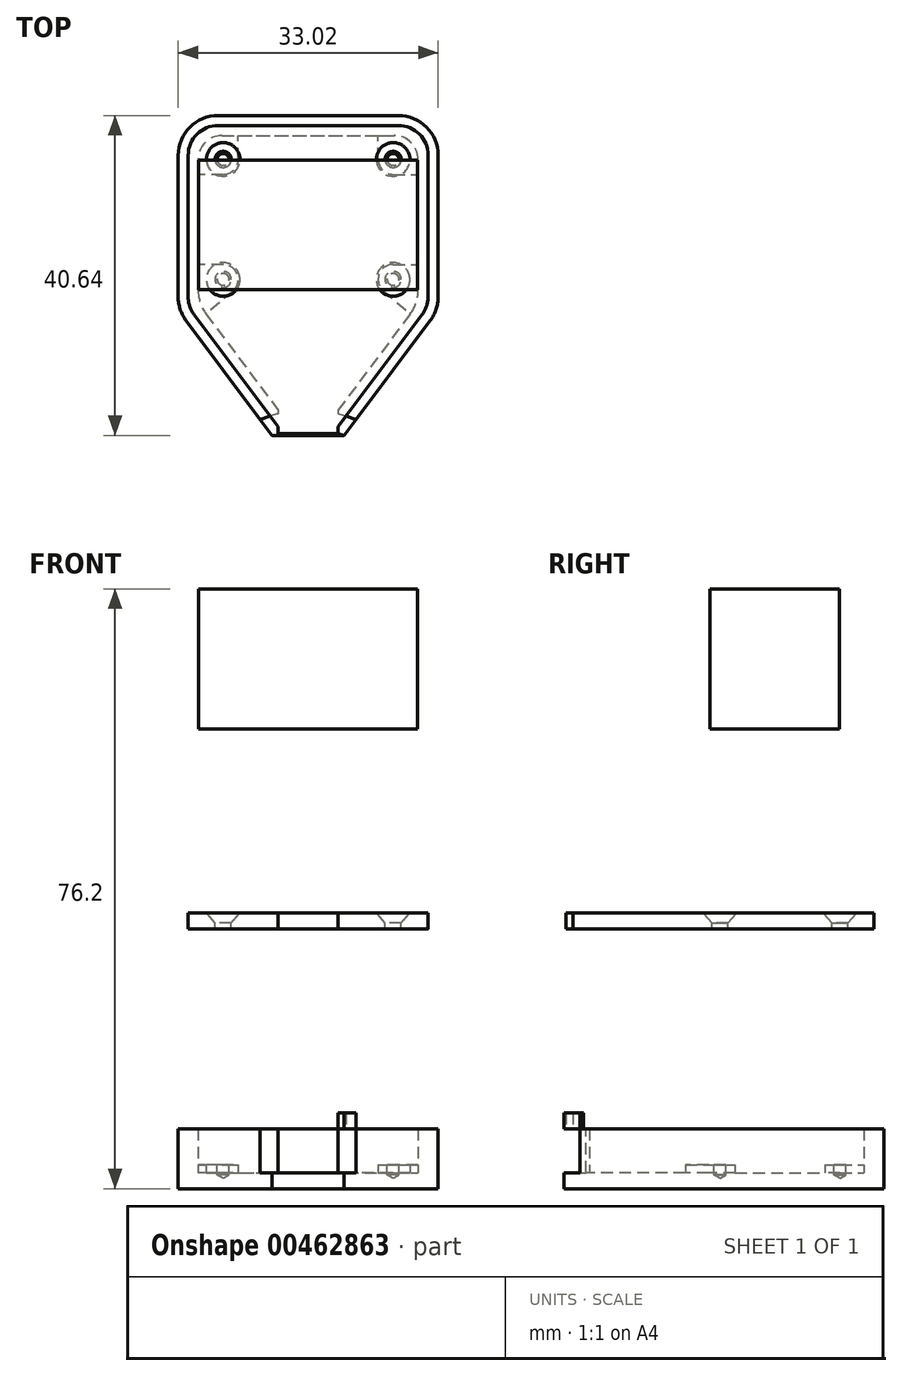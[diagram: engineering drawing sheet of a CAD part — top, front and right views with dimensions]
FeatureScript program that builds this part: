
annotation { "Feature Type Name" : "Feature", "Feature Type Description" : "" }
export const myFeature = defineFeature(function(context is Context, id is Id, definition is map)
    precondition{}
    {
        {
            var Q0;
            Q0=qCreatedBy(makeId("Top.planeOp"),FACE);
            var sketch = newSketch(context, id + "F0", { "sketchPlane" : qUnion([Q0])});
            skLineSegment(sketch, "E0.right", {"start": v(-13.97, -10.67) * mm, "end": v(-13.97, 10.67) * mm});
            skLineSegment(sketch, "E1", {"start": v(-13.97, -10.67) * mm, "end": v(-3.81, -24.21) * mm});
            skLineSegment(sketch, "E2", {"start": v(-3.81, -24.21) * mm, "end": v(-3.81, -28.45) * mm});
            skLineSegment(sketch, "E3", {"start": v(-3.8, -28.45) * mm, "end": v(-16.51, -11.51) * mm});
            skLineSegment(sketch, "E4", {"start": v(-16.51, -11.51) * mm, "end": v(-16.51, 13.2) * mm});
            skLineSegment(sketch, "E5", {"start": v(-13.97, 10.67) * mm, "end": v(0, 10.67) * mm});
            skLineSegment(sketch, "E6", {"start": v(-16.51, 13.2) * mm, "end": v(0, 13.2) * mm});
            skLineSegment(sketch, "E7", {"start": v(0, 10.67) * mm, "end": v(0, 13.2) * mm, "construction": true});
            skLineSegment(sketch, "E8", {"start": v(-13.97, 0) * mm, "end": v(-16.51, 0) * mm, "construction": true});
            skLineSegment(sketch, "E9", {"start": v(-8.9, -17.44) * mm, "end": v(-10.92, -18.97) * mm, "construction": true});
            skLineSegment(sketch, "E10", {"start": v(-13.97, -10.67) * mm, "end": v(0, -10.67) * mm, "construction": true});
            skLineSegment(sketch, "E11", {"start": v(0, -10.67) * mm, "end": v(0, -28.45) * mm, "construction": true});
            skLineSegment(sketch, "E12", {"start": v(0, -28.45) * mm, "end": v(-3.8, -28.45) * mm});
            skLineSegment(sketch, "E13", {"start": v(0, 10.16) * mm, "end": v(0, -10.67) * mm, "construction": true});
            skLineSegment(sketch, "E14.MirrorCS", {"start": v(16.51, 13.2) * mm, "end": v(0, 13.2) * mm});
            skLineSegment(sketch, "E15.MirrorCS", {"start": v(13.97, 10.67) * mm, "end": v(0, 10.67) * mm});
            skLineSegment(sketch, "E16.MirrorCS", {"start": v(16.51, -11.51) * mm, "end": v(16.51, 13.2) * mm});
            skLineSegment(sketch, "E17.MirrorCS", {"start": v(13.97, -10.67) * mm, "end": v(13.97, 10.67) * mm});
            skLineSegment(sketch, "E18.MirrorCS", {"start": v(13.97, -10.67) * mm, "end": v(3.81, -24.21) * mm});
            skLineSegment(sketch, "E19.MirrorCS", {"start": v(3.8, -28.45) * mm, "end": v(16.51, -11.51) * mm});
            skLineSegment(sketch, "E20.MirrorCS", {"start": v(3.81, -24.21) * mm, "end": v(3.81, -28.45) * mm});
            skLineSegment(sketch, "E21.MirrorCS", {"start": v(0, -28.45) * mm, "end": v(3.81, -28.45) * mm});
            skLineSegment(sketch, "E22", {"start": v(13.46, 0) * mm, "end": v(-13.46, 0) * mm, "construction": true});
            skLineSegment(sketch, "E23", {"start": v(-3.81, -24.21) * mm, "end": v(3.81, -24.21) * mm, "construction": true});
            skLineSegment(sketch, "E24", {"start": v(-13.46, 7.62) * mm, "end": v(-10.8, 7.62) * mm, "construction": true});
            skLineSegment(sketch, "E25", {"start": v(-10.8, 7.62) * mm, "end": v(-10.8, 10.16) * mm, "construction": true});
            skLineSegment(sketch, "E26.bottom", {"start": v(-10.92, 10.16) * mm, "end": v(13.46, 10.16) * mm, "construction": true});
            skLineSegment(sketch, "E26.top", {"start": v(-13.46, -10.16) * mm, "end": v(13.46, -10.16) * mm, "construction": true});
            skLineSegment(sketch, "E26.left", {"start": v(-13.46, 7.62) * mm, "end": v(-13.46, -10.16) * mm, "construction": true});
            skLineSegment(sketch, "E26.right", {"start": v(13.46, 10.16) * mm, "end": v(13.46, -10.16) * mm, "construction": true});
            skPoint(sketch, "E26.middle", {"position": v(0, 0) * mm});
            skLineSegment(sketch, "E27", {"start": v(-13.46, 0) * mm, "end": v(-13.97, 0) * mm, "construction": true});
            skLineSegment(sketch, "E28.bottom", {"start": v(0, 10.67) * mm, "end": v(0, 10.67) * mm});
            skLineSegment(sketch, "E28.top", {"start": v(0, 10.16) * mm, "end": v(0, 10.16) * mm});
            skLineSegment(sketch, "E28.left", {"start": v(0, 10.67) * mm, "end": v(0, 10.16) * mm, "construction": true});
            skLineSegment(sketch, "E28.right", {"start": v(0, 10.67) * mm, "end": v(0, 10.16) * mm, "construction": true});
            skPoint(sketch, "E29.visualSharp", {"position": v(-13.46, 10.16) * mm});
            skArc(sketch, "E29.filletArc", {"start": v(-10.92, 10.16) * mm, "mid": v(-12.72, 9.42) * mm, "end": v(-13.46, 7.62) * mm, "construction": true});
            skSolve(sketch);
        }
        {
            var Q0;
            Q0=makeQuery(id+"F0.imprint","IMPRINT",FACE,{"disambiguationData":[TD([[makeQuery(id+"F0.imprint","IMPRINT",EDGE,{"derivedFrom":sQuery(id+"F0.wireOp",EDGE,"E0.right")}),1.0]])]});
            extrude(context, id + "F1", {"entities" : qUnion([Q0]), "depth" : 5.6 * mm});
        }
        {
            var Q0;
            {var subQ0=sQuery(id+"F0.wireOp",EDGE,"E16.MirrorCS");var subQ1=sQuery(id+"F0.wireOp",EDGE,"E14.MirrorCS");Q0=makeQuery(id+"F1.boolean.opBoolean","MERGE",EDGE,{"derivedFrom":[makeQuery(id+"Ff96gasZhOdMvVI_0.opExtrude","SWEPT_EDGE",EDGE,{"disambiguationData":[OSD([subQ1,subQ0])]}),makeQuery(id+"F1.opExtrude","SWEPT_EDGE",EDGE,{"disambiguationData":[OSD([subQ1,subQ0])]})]});}
            var Q1;
            {var subQ0=sQuery(id+"F0.wireOp",EDGE,"E6");var subQ1=sQuery(id+"F0.wireOp",EDGE,"E4");Q1=makeQuery(id+"F1.boolean.opBoolean","MERGE",EDGE,{"derivedFrom":[makeQuery(id+"Ff96gasZhOdMvVI_0.opExtrude","SWEPT_EDGE",EDGE,{"disambiguationData":[OSD([subQ1,subQ0])]}),makeQuery(id+"F1.opExtrude","SWEPT_EDGE",EDGE,{"disambiguationData":[OSD([subQ1,subQ0])]})]});}
            var Q2;
            {var subQ0=sQuery(id+"F0.wireOp",EDGE,"E19.MirrorCS");var subQ1=sQuery(id+"F0.wireOp",EDGE,"E16.MirrorCS");Q2=makeQuery(id+"F1.boolean.opBoolean","MERGE",EDGE,{"derivedFrom":[makeQuery(id+"Ff96gasZhOdMvVI_0.opExtrude","SWEPT_EDGE",EDGE,{"disambiguationData":[OSD([subQ1,subQ0])]}),makeQuery(id+"F1.opExtrude","SWEPT_EDGE",EDGE,{"disambiguationData":[OSD([subQ1,subQ0])]})]});}
            var Q3;
            Q3=makeQuery(id+"F1.opExtrude","SWEPT_EDGE",EDGE,{"disambiguationData":[OSD([sQuery(id+"F0.wireOp",EDGE,"E0.right"),sQuery(id+"F0.wireOp",EDGE,"E1")])]});
            var Q4;
            Q4=makeQuery(id+"F1.opExtrude","SWEPT_EDGE",EDGE,{"disambiguationData":[OSD([sQuery(id+"F0.wireOp",EDGE,"E17.MirrorCS"),sQuery(id+"F0.wireOp",EDGE,"E18.MirrorCS")])]});
            var Q5;
            {var subQ0=sQuery(id+"F0.wireOp",EDGE,"E4");var subQ1=sQuery(id+"F0.wireOp",EDGE,"E3");Q5=makeQuery(id+"F1.boolean.opBoolean","MERGE",EDGE,{"derivedFrom":[makeQuery(id+"Ff96gasZhOdMvVI_0.opExtrude","SWEPT_EDGE",EDGE,{"disambiguationData":[OSD([subQ1,subQ0])]}),makeQuery(id+"F1.opExtrude","SWEPT_EDGE",EDGE,{"disambiguationData":[OSD([subQ1,subQ0])]})]});}
            fillet(context, id + "F2", {"entities" : qUnion([Q0, Q1, Q2, Q3, Q4, Q5]), "radius" : 5.08 * mm, "tangentPropagation" : true, "allowEdgeOverflow" : false});
        }
        {
            var Q0;
            Q0=makeQuery(id+"F1.opExtrude","SWEPT_EDGE",EDGE,{"disambiguationData":[OSD([sQuery(id+"F0.wireOp",EDGE,"E0.right"),sQuery(id+"F0.wireOp",EDGE,"E5")])]});
            var Q1;
            Q1=makeQuery(id+"F1.opExtrude","SWEPT_EDGE",EDGE,{"disambiguationData":[OSD([sQuery(id+"F0.wireOp",EDGE,"E15.MirrorCS"),sQuery(id+"F0.wireOp",EDGE,"E17.MirrorCS")])]});
            fillet(context, id + "F3", {"entities" : qUnion([Q0, Q1]), "radius" : 3.05 * mm, "tangentPropagation" : true, "allowEdgeOverflow" : false});
        }
        {
            var Q0;
            Q0=makeQuery(id+"F1.opExtrude","SWEPT_EDGE",EDGE,{"disambiguationData":[OSD([sQuery(id+"F0.wireOp",EDGE,"E19.MirrorCS"),sQuery(id+"F0.wireOp",EDGE,"E20.MirrorCS"),sQuery(id+"F0.wireOp",EDGE,"E21.MirrorCS")])]});
            var Q1;
            Q1=makeQuery(id+"F1.opExtrude","SWEPT_EDGE",EDGE,{"disambiguationData":[OSD([sQuery(id+"F0.wireOp",EDGE,"E2"),sQuery(id+"F0.wireOp",EDGE,"E3"),sQuery(id+"F0.wireOp",EDGE,"E12")])]});
            chamfer(context, id + "F4", {"entities" : qUnion([Q0, Q1]), "width" : 1.27 * mm, "tangentPropagation" : true});
        }
        {
            var Q0;
            Q0=makeQuery(id+"F1.opExtrude","CAP_FACE",FACE,{"disambiguationData":[OSD([sQuery(id+"F0.wireOp",EDGE,"E0.right"),sQuery(id+"F0.wireOp",EDGE,"E1"),sQuery(id+"F0.wireOp",EDGE,"E2"),sQuery(id+"F0.wireOp",EDGE,"E3"),sQuery(id+"F0.wireOp",EDGE,"E4"),sQuery(id+"F0.wireOp",EDGE,"E5"),sQuery(id+"F0.wireOp",EDGE,"E6"),sQuery(id+"F0.wireOp",EDGE,"E14.MirrorCS"),sQuery(id+"F0.wireOp",EDGE,"E15.MirrorCS"),sQuery(id+"F0.wireOp",EDGE,"E16.MirrorCS"),sQuery(id+"F0.wireOp",EDGE,"E17.MirrorCS"),sQuery(id+"F0.wireOp",EDGE,"E18.MirrorCS"),sQuery(id+"F0.wireOp",EDGE,"E19.MirrorCS"),sQuery(id+"F0.wireOp",EDGE,"E20.MirrorCS")])],"isStart":true});
            var sketch = newSketch(context, id + "F5", { "sketchPlane" : qUnion([Q0])});
            skArc(sketch, "E30.0", {"start": v(16.51, 9.82) * mm, "mid": v(16.25, 11.43) * mm, "end": v(15.5, 12.87) * mm});
            skLineSegment(sketch, "E31.0", {"start": v(16.51, 9.82) * mm, "end": v(16.51, -8.13) * mm});
            skArc(sketch, "E32.0", {"start": v(11.43, -13.2) * mm, "mid": v(15.02, -11.72) * mm, "end": v(16.51, -8.13) * mm});
            skLineSegment(sketch, "E33.0", {"start": v(11.43, -13.2) * mm, "end": v(-11.43, -13.2) * mm});
            skArc(sketch, "E34.0", {"start": v(-16.51, -8.13) * mm, "mid": v(-15.02, -11.72) * mm, "end": v(-11.43, -13.2) * mm});
            skLineSegment(sketch, "E35.0", {"start": v(-16.51, 9.82) * mm, "end": v(-16.51, -8.13) * mm});
            skArc(sketch, "E36.0", {"start": v(-15.5, 12.87) * mm, "mid": v(-16.25, 11.43) * mm, "end": v(-16.51, 9.82) * mm});
            skLineSegment(sketch, "E37.0", {"start": v(4.57, 27.43) * mm, "end": v(15.5, 12.87) * mm});
            skLineSegment(sketch, "E38.0", {"start": v(-4.57, 27.43) * mm, "end": v(-15.5, 12.87) * mm});
            skLineSegment(sketch, "E39", {"start": v(4.57, 27.43) * mm, "end": v(-4.57, 27.43) * mm});
            skSolve(sketch);
        }
        {
            var Q0;
            Q0 = qSketchRegion(id + "F5", true);
            extrude(context, id + "F6", {"entities" : qUnion([Q0]), "operationType" : NewBodyOperationType.ADD, "depth" : 2.03 * mm});
        }
        {
            var Q0;
            Q0=makeQuery(id+"F1.opExtrude","CAP_FACE",FACE,{"disambiguationData":[OSD([sQuery(id+"F0.wireOp",EDGE,"E0.right"),sQuery(id+"F0.wireOp",EDGE,"E1"),sQuery(id+"F0.wireOp",EDGE,"E2"),sQuery(id+"F0.wireOp",EDGE,"E3"),sQuery(id+"F0.wireOp",EDGE,"E4"),sQuery(id+"F0.wireOp",EDGE,"E5"),sQuery(id+"F0.wireOp",EDGE,"E6"),sQuery(id+"F0.wireOp",EDGE,"E14.MirrorCS"),sQuery(id+"F0.wireOp",EDGE,"E15.MirrorCS"),sQuery(id+"F0.wireOp",EDGE,"E16.MirrorCS"),sQuery(id+"F0.wireOp",EDGE,"E17.MirrorCS"),sQuery(id+"F0.wireOp",EDGE,"E18.MirrorCS"),sQuery(id+"F0.wireOp",EDGE,"E19.MirrorCS"),sQuery(id+"F0.wireOp",EDGE,"E20.MirrorCS")])],"isStart":false});
            var sketch = newSketch(context, id + "F7", { "sketchPlane" : qUnion([Q0])});
            skLineSegment(sketch, "E40.0", {"start": v(4.57, -27.43) * mm, "end": v(15.5, -12.87) * mm});
            skArc(sketch, "E41.0", {"start": v(15.5, -12.87) * mm, "mid": v(16.25, -11.43) * mm, "end": v(16.51, -9.82) * mm});
            skLineSegment(sketch, "E42.0", {"start": v(16.51, -9.82) * mm, "end": v(16.51, 8.13) * mm});
            skArc(sketch, "E43.0", {"start": v(16.51, 8.13) * mm, "mid": v(15.02, 11.72) * mm, "end": v(11.43, 13.2) * mm});
            skLineSegment(sketch, "E44.0", {"start": v(11.43, 13.2) * mm, "end": v(-11.43, 13.2) * mm});
            skArc(sketch, "E45.0", {"start": v(-11.43, 13.2) * mm, "mid": v(-15.02, 11.72) * mm, "end": v(-16.51, 8.13) * mm});
            skLineSegment(sketch, "E46.0", {"start": v(-16.51, -9.82) * mm, "end": v(-16.51, 8.13) * mm});
            skArc(sketch, "E47.0", {"start": v(-16.51, -9.82) * mm, "mid": v(-16.25, -11.43) * mm, "end": v(-15.5, -12.87) * mm});
            skLineSegment(sketch, "E48.0", {"start": v(-4.57, -27.43) * mm, "end": v(-15.5, -12.87) * mm});
            skLineSegment(sketch, "E49", {"start": v(-4.57, -27.43) * mm, "end": v(-3.81, -27.18) * mm});
            skLineSegment(sketch, "E50", {"start": v(3.81, -27.18) * mm, "end": v(4.57, -27.43) * mm});
            skLineSegment(sketch, "E51.0", {"start": v(3.81, -26.33) * mm, "end": v(14.48, -12.1) * mm});
            skArc(sketch, "E51.1", {"start": v(14.48, -12.1) * mm, "mid": v(15.04, -11.03) * mm, "end": v(15.24, -9.82) * mm});
            skLineSegment(sketch, "E51.2", {"start": v(15.24, -9.82) * mm, "end": v(15.24, 8.13) * mm});
            skArc(sketch, "E51.3", {"start": v(15.24, 8.13) * mm, "mid": v(14.12, 10.82) * mm, "end": v(11.43, 11.94) * mm});
            skLineSegment(sketch, "E51.4", {"start": v(11.43, 11.94) * mm, "end": v(-11.43, 11.94) * mm});
            skLineSegment(sketch, "E51.5", {"start": v(-3.81, -26.33) * mm, "end": v(-14.48, -12.1) * mm});
            skArc(sketch, "E51.6", {"start": v(-15.24, -9.82) * mm, "mid": v(-15.04, -11.03) * mm, "end": v(-14.48, -12.1) * mm});
            skLineSegment(sketch, "E51.7", {"start": v(-15.24, -9.82) * mm, "end": v(-15.24, 8.13) * mm});
            skArc(sketch, "E51.8", {"start": v(-11.43, 11.94) * mm, "mid": v(-14.12, 10.82) * mm, "end": v(-15.24, 8.13) * mm});
            skLineSegment(sketch, "E52", {"start": v(-3.8, -26.33) * mm, "end": v(-3.8, -27.18) * mm});
            skLineSegment(sketch, "E53", {"start": v(3.8, -26.33) * mm, "end": v(3.81, -27.18) * mm});
            skSolve(sketch);
        }
        {
            var Q0;
            Q0=makeQuery(id+"F7.imprint","IMPRINT",FACE,{"disambiguationData":[TD([[makeQuery(id+"F7.imprint","IMPRINT",EDGE,{"derivedFrom":sQuery(id+"F7.wireOp",EDGE,"E40.0")}),1.0]])]});
            extrude(context, id + "F8", {"entities" : qUnion([Q0]), "operationType" : NewBodyOperationType.ADD, "depth" : 2.03 * mm});
        }
        {
            var Q0;
            Q0=makeQuery(id+"F6.opExtrude","CAP_FACE",FACE,{"disambiguationData":[OSD([sQuery(id+"F5.wireOp",EDGE,"614055ea-427b-4cb9-ac48-1e12848c68dc.0"),sQuery(id+"F5.wireOp",EDGE,"E30.0"),sQuery(id+"F5.wireOp",EDGE,"E31.0"),sQuery(id+"F5.wireOp",EDGE,"E32.0"),sQuery(id+"F5.wireOp",EDGE,"E33.0"),sQuery(id+"F5.wireOp",EDGE,"E34.0"),sQuery(id+"F5.wireOp",EDGE,"E35.0"),sQuery(id+"F5.wireOp",EDGE,"E36.0"),sQuery(id+"F5.wireOp",EDGE,"936ec802-ce90-48c8-9038-d904150573fe.0"),sQuery(id+"F5.wireOp",EDGE,"719f3388-4424-430d-82b7-2a579ba14330.0"),sQuery(id+"F5.wireOp",EDGE,"24262252-db0e-4c5c-9644-e6070294630f.0"),sQuery(id+"F5.wireOp",EDGE,"891P9168-ehHu-ZQn1-B7PZ-iqxXZud2gJmg")])],"isStart":true});
            var sketch = newSketch(context, id + "F9", { "sketchPlane" : qUnion([Q0])});
            skPoint(sketch, "E54.0", {"position": v(-10.8, 7.62) * mm});
            skLineSegment(sketch, "E55.0", {"start": v(0, 10.16) * mm, "end": v(0, -10.67) * mm, "construction": true});
            skLineSegment(sketch, "E56.0", {"start": v(13.46, 0) * mm, "end": v(-13.46, 0) * mm, "construction": true});
            skCircle(sketch, "E57", {"center": v(-10.8, 7.62) * mm, "radius": 1.9 * mm});
            skCircle(sketch, "E58.MirrorC", {"center": v(10.8, 7.62) * mm, "radius": 1.9 * mm});
            skCircle(sketch, "E59.MirrorC", {"center": v(-10.8, -7.62) * mm, "radius": 1.9 * mm});
            skCircle(sketch, "E60.MirrorC", {"center": v(10.8, -7.62) * mm, "radius": 1.9 * mm});
            skLineSegment(sketch, "E61", {"start": v(-8.9, 7.62) * mm, "end": v(-8.9, 10.67) * mm});
            skLineSegment(sketch, "E62", {"start": v(-10.8, 5.71) * mm, "end": v(-13.97, 5.71) * mm});
            skLineSegment(sketch, "E63", {"start": v(-10.8, -5.72) * mm, "end": v(-13.97, -5.72) * mm});
            skLineSegment(sketch, "E64", {"start": v(-9.54, -9.06) * mm, "end": v(-12.95, -12.02) * mm});
            skLineSegment(sketch, "E65.MirrorCS", {"start": v(8.9, 7.62) * mm, "end": v(8.9, 10.67) * mm});
            skLineSegment(sketch, "E66.MirrorCS", {"start": v(10.8, 5.71) * mm, "end": v(13.97, 5.71) * mm});
            skLineSegment(sketch, "E67.MirrorCS", {"start": v(10.8, -5.72) * mm, "end": v(13.97, -5.72) * mm});
            skLineSegment(sketch, "E68.MirrorCS", {"start": v(9.54, -9.06) * mm, "end": v(12.95, -12.02) * mm});
            skCircle(sketch, "E69", {"center": v(-10.8, 7.62) * mm, "radius": 1.14 * mm, "construction": true});
            skCircle(sketch, "E70.MirrorC", {"center": v(10.8, 7.62) * mm, "radius": 1.14 * mm, "construction": true});
            skCircle(sketch, "E71.MirrorC", {"center": v(-10.8, -7.62) * mm, "radius": 1.14 * mm, "construction": true});
            skCircle(sketch, "E72.MirrorC", {"center": v(10.8, -7.62) * mm, "radius": 1.14 * mm, "construction": true});
            skPoint(sketch, "E73", {"position": v(-9.65, 7.62) * mm});
            skPoint(sketch, "E74", {"position": v(-10.8, 8.76) * mm});
            skPoint(sketch, "E75", {"position": v(-10.8, 6.48) * mm});
            skPoint(sketch, "E76", {"position": v(-11.94, 7.62) * mm});
            skPoint(sketch, "E77.MirrorP", {"position": v(11.94, 7.62) * mm});
            skPoint(sketch, "E78.MirrorP", {"position": v(10.8, 8.76) * mm});
            skPoint(sketch, "E79.MirrorP", {"position": v(10.8, 6.48) * mm});
            skPoint(sketch, "E80.MirrorP", {"position": v(9.65, 7.62) * mm});
            skPoint(sketch, "E81.MirrorP", {"position": v(10.8, -8.76) * mm});
            skPoint(sketch, "E82.MirrorP", {"position": v(11.94, -7.62) * mm});
            skPoint(sketch, "E83.MirrorP", {"position": v(10.8, -6.48) * mm});
            skPoint(sketch, "E84.MirrorP", {"position": v(9.65, -7.62) * mm});
            skPoint(sketch, "E85.MirrorP", {"position": v(-10.8, -6.48) * mm});
            skPoint(sketch, "E86.MirrorP", {"position": v(-11.94, -7.62) * mm});
            skPoint(sketch, "E87.MirrorP", {"position": v(-10.8, -8.76) * mm});
            skPoint(sketch, "E88.MirrorP", {"position": v(-9.65, -7.62) * mm});
            skSolve(sketch);
        }
        {
            var Q0;
            Q0 = qSketchRegion(id + "F9", true);
            var Q1;
            {var subQ4=sQuery(id+"F9.wireOp",EDGE,"E67.MirrorCS");Q1=makeQuery(id+"F9.imprint","IMPRINT",FACE,{"disambiguationData":[TD([[makeQuery(id+"F9.imprint","IMPRINT",EDGE,{"derivedFrom":subQ4}),-1.0]])]});}
            var Q2;
            {var subQ1=sQuery(id+"F9.wireOp",EDGE,"E65.MirrorCS");Q2=makeQuery(id+"F9.imprint","IMPRINT",FACE,{"disambiguationData":[TD([[makeQuery(id+"F9.imprint","IMPRINT",EDGE,{"derivedFrom":subQ1}),-1.0]])]});}
            var Q3;
            {var subQ6=sQuery(id+"F9.wireOp",EDGE,"E61");Q3=makeQuery(id+"F9.imprint","IMPRINT",FACE,{"disambiguationData":[TD([[makeQuery(id+"F9.imprint","IMPRINT",EDGE,{"derivedFrom":subQ6}),1.0]])]});}
            var Q4;
            {var subQ4=sQuery(id+"F9.wireOp",EDGE,"E63");Q4=makeQuery(id+"F9.imprint","IMPRINT",FACE,{"disambiguationData":[TD([[makeQuery(id+"F9.imprint","IMPRINT",EDGE,{"derivedFrom":subQ4}),1.0]])]});}
            extrude(context, id + "F10", {"entities" : qUnion([Q0, Q1, Q2, Q3, Q4]), "operationType" : NewBodyOperationType.ADD, "depth" : 1.02 * mm});
        }
        {
            var Q0;
            Q0=makeQuery(id+"F1.opExtrude","CAP_FACE",FACE,{"disambiguationData":[OSD([sQuery(id+"F0.wireOp",EDGE,"E0.right"),sQuery(id+"F0.wireOp",EDGE,"E1"),sQuery(id+"F0.wireOp",EDGE,"E2"),sQuery(id+"F0.wireOp",EDGE,"E3"),sQuery(id+"F0.wireOp",EDGE,"E4"),sQuery(id+"F0.wireOp",EDGE,"E5"),sQuery(id+"F0.wireOp",EDGE,"E6"),sQuery(id+"F0.wireOp",EDGE,"E14.MirrorCS"),sQuery(id+"F0.wireOp",EDGE,"E15.MirrorCS"),sQuery(id+"F0.wireOp",EDGE,"E16.MirrorCS"),sQuery(id+"F0.wireOp",EDGE,"E17.MirrorCS"),sQuery(id+"F0.wireOp",EDGE,"E18.MirrorCS"),sQuery(id+"F0.wireOp",EDGE,"E19.MirrorCS"),sQuery(id+"F0.wireOp",EDGE,"E20.MirrorCS")])],"isStart":false});
            var sketch = newSketch(context, id + "F11", { "sketchPlane" : qUnion([Q0])});
            skLineSegment(sketch, "E89", {"start": v(-15.24, 8.13) * mm, "end": v(-15.24, -9.82) * mm});
            skArc(sketch, "E90", {"start": v(-15.24, 8.13) * mm, "mid": v(-14.12, 10.82) * mm, "end": v(-11.43, 11.94) * mm});
            skLineSegment(sketch, "E91", {"start": v(-11.43, 11.94) * mm, "end": v(11.43, 11.94) * mm});
            skArc(sketch, "E92", {"start": v(-14.48, -12.1) * mm, "mid": v(-15.04, -11.03) * mm, "end": v(-15.24, -9.82) * mm});
            skLineSegment(sketch, "E93", {"start": v(-14.48, -12.1) * mm, "end": v(-3.8, -26.33) * mm});
            skArc(sketch, "E94", {"start": v(11.43, 11.94) * mm, "mid": v(14.12, 10.82) * mm, "end": v(15.24, 8.13) * mm});
            skLineSegment(sketch, "E95", {"start": v(15.24, 8.13) * mm, "end": v(15.24, -9.82) * mm});
            skArc(sketch, "E96", {"start": v(15.24, -9.82) * mm, "mid": v(15.04, -11.03) * mm, "end": v(14.48, -12.1) * mm});
            skLineSegment(sketch, "E97", {"start": v(14.48, -12.1) * mm, "end": v(3.81, -26.33) * mm});
            skPoint(sketch, "E98.0", {"position": v(-3.81, -27.18) * mm});
            skPoint(sketch, "E99.0", {"position": v(3.81, -27.18) * mm});
            skLineSegment(sketch, "E100", {"start": v(-3.8, -26.33) * mm, "end": v(-3.81, -27.18) * mm});
            skLineSegment(sketch, "E101", {"start": v(-3.81, -27.18) * mm, "end": v(3.81, -27.18) * mm});
            skLineSegment(sketch, "E102", {"start": v(3.81, -27.18) * mm, "end": v(3.81, -26.33) * mm});
            skSolve(sketch);
        }
        {
            var Q0;
            Q0 = qSketchRegion(id + "F11", true);
            var Q1;
            Q1=makeQuery(id+"F8.opExtrude","CAP_FACE",FACE,{"disambiguationData":[OSD([sQuery(id+"F7.wireOp",EDGE,"E40.0"),sQuery(id+"F7.wireOp",EDGE,"E41.0"),sQuery(id+"F7.wireOp",EDGE,"E42.0"),sQuery(id+"F7.wireOp",EDGE,"E43.0"),sQuery(id+"F7.wireOp",EDGE,"E44.0"),sQuery(id+"F7.wireOp",EDGE,"E45.0"),sQuery(id+"F7.wireOp",EDGE,"E46.0"),sQuery(id+"F7.wireOp",EDGE,"E47.0"),sQuery(id+"F7.wireOp",EDGE,"E48.0"),sQuery(id+"F7.wireOp",EDGE,"E49"),sQuery(id+"F7.wireOp",EDGE,"E50"),sQuery(id+"F7.wireOp",EDGE,"E51.0"),sQuery(id+"F7.wireOp",EDGE,"E51.1"),sQuery(id+"F7.wireOp",EDGE,"E51.2"),sQuery(id+"F7.wireOp",EDGE,"E51.3"),sQuery(id+"F7.wireOp",EDGE,"E51.4"),sQuery(id+"F7.wireOp",EDGE,"E51.5"),sQuery(id+"F7.wireOp",EDGE,"E51.6"),sQuery(id+"F7.wireOp",EDGE,"E51.7"),sQuery(id+"F7.wireOp",EDGE,"E51.8"),sQuery(id+"F7.wireOp",EDGE,"E52"),sQuery(id+"F7.wireOp",EDGE,"E53")])],"isStart":false});
            extrude(context, id + "F12", {"entities" : qUnion([Q0]), "endBound" : BoundingType.UP_TO_SURFACE, "endBoundEntityFace" : qUnion([Q1]), "depth" : 25.4 * mm});
        }
        {
            var Q0;
            Q0=makeQuery(id+"F12.opExtrude","CAP_FACE",FACE,{"disambiguationData":[OSD([sQuery(id+"F11.wireOp",EDGE,"E89"),sQuery(id+"F11.wireOp",EDGE,"E90"),sQuery(id+"F11.wireOp",EDGE,"E91"),sQuery(id+"F11.wireOp",EDGE,"E92"),sQuery(id+"F11.wireOp",EDGE,"E93"),sQuery(id+"F11.wireOp",EDGE,"E94"),sQuery(id+"F11.wireOp",EDGE,"E95"),sQuery(id+"F11.wireOp",EDGE,"E96"),sQuery(id+"F11.wireOp",EDGE,"E97"),sQuery(id+"F11.wireOp",EDGE,"E100"),sQuery(id+"F11.wireOp",EDGE,"E101"),sQuery(id+"F11.wireOp",EDGE,"E102")])],"isStart":false});
            var sketch = newSketch(context, id + "F13", { "sketchPlane" : qUnion([Q0])});
            skCircle(sketch, "E103.0", {"center": v(-10.8, 7.62) * mm, "radius": 1.9 * mm, "construction": true});
            skCircle(sketch, "E104.0", {"center": v(-10.8, -7.62) * mm, "radius": 1.9 * mm, "construction": true});
            skCircle(sketch, "E105.0", {"center": v(10.8, 7.62) * mm, "radius": 1.9 * mm, "construction": true});
            skCircle(sketch, "E106.0", {"center": v(10.8, -7.62) * mm, "radius": 1.9 * mm, "construction": true});
            skSolve(sketch);
        }
        {
            var Q0;
            Q0=sQuery(id+"F13.wireOp",VERTEX,"E106.0.center");
            var Q1;
            Q1=sQuery(id+"F13.wireOp",VERTEX,"E104.0.center");
            var Q2;
            Q2=sQuery(id+"F13.wireOp",VERTEX,"E103.0.center");
            var Q3;
            Q3=sQuery(id+"F13.wireOp",VERTEX,"E105.0.center");
            var Q4;
            Q4=makeQuery(id+"F12.opExtrude","SWEPT_BODY",BODY,{"disambiguationData":[OSD([sQuery(id+"F11.wireOp",EDGE,"E89"),sQuery(id+"F11.wireOp",EDGE,"E90"),sQuery(id+"F11.wireOp",EDGE,"E91"),sQuery(id+"F11.wireOp",EDGE,"E92"),sQuery(id+"F11.wireOp",EDGE,"E93"),sQuery(id+"F11.wireOp",EDGE,"E94"),sQuery(id+"F11.wireOp",EDGE,"E95"),sQuery(id+"F11.wireOp",EDGE,"E96"),sQuery(id+"F11.wireOp",EDGE,"E97"),sQuery(id+"F11.wireOp",EDGE,"TcZf5NMe-sSkd-wtcx-RJIe-wvG45Bildv15")])]});
            var Q5;
            Q5=makeQuery(id+"F1.opExtrude","SWEPT_BODY",BODY,{"disambiguationData":[OSD([sQuery(id+"F0.wireOp",EDGE,"E0.right"),sQuery(id+"F0.wireOp",EDGE,"E1"),sQuery(id+"F0.wireOp",EDGE,"E2"),sQuery(id+"F0.wireOp",EDGE,"E3"),sQuery(id+"F0.wireOp",EDGE,"E4"),sQuery(id+"F0.wireOp",EDGE,"E5"),sQuery(id+"F0.wireOp",EDGE,"E6"),sQuery(id+"F0.wireOp",EDGE,"E14.MirrorCS"),sQuery(id+"F0.wireOp",EDGE,"E15.MirrorCS"),sQuery(id+"F0.wireOp",EDGE,"E16.MirrorCS"),sQuery(id+"F0.wireOp",EDGE,"E17.MirrorCS"),sQuery(id+"F0.wireOp",EDGE,"E18.MirrorCS"),sQuery(id+"F0.wireOp",EDGE,"E19.MirrorCS"),sQuery(id+"F0.wireOp",EDGE,"E20.MirrorCS")])]});
            hole(context, id + "F14", {"style" : HoleStyle.C_SINK, "endStyle" : HoleEndStyle.BLIND_IN_LAST, "standardTappedOrClearance" : lookupTablePath({ "fit" : "Normal", "standard" : "ANSI", "engagement" : "75%", "pitch" : "64 tpi", "size" : "#1", "type" : "Clearance & tapped" }), "standardBlindInLast" : lookupTablePath({ "standard" : "ANSI", "fit" : "Free", "engagement" : "75%", "pitch" : "64 tpi", "size" : "#1", "type" : "Clearance & tapped" }), "holeDiameter" : 2.06 * mm, "cSinkDiameter" : 4.27 * mm, "cSinkAngle" : 82 * degree, "tapDrillDiameter" : 1.51 * mm, "showTappedDepth" : true, "holeDepth" : 1.27 * mm, "isTappedThrough" : true, "tappedDepth" : 0.08 * mm, "tapClearance" : 3, "locations" : qUnion([Q0, Q1, Q2, Q3]), "scope" : qUnion([Q4, Q5]), "majorDiameter" : 1.85 * mm});
        }
        {
            var Q0;
            Q0=makeQuery(id+"F1.opExtrude","CAP_FACE",FACE,{"disambiguationData":[OSD([sQuery(id+"F0.wireOp",EDGE,"E0.right"),sQuery(id+"F0.wireOp",EDGE,"E1"),sQuery(id+"F0.wireOp",EDGE,"E2"),sQuery(id+"F0.wireOp",EDGE,"E3"),sQuery(id+"F0.wireOp",EDGE,"E4"),sQuery(id+"F0.wireOp",EDGE,"E5"),sQuery(id+"F0.wireOp",EDGE,"E6"),sQuery(id+"F0.wireOp",EDGE,"E14.MirrorCS"),sQuery(id+"F0.wireOp",EDGE,"E15.MirrorCS"),sQuery(id+"F0.wireOp",EDGE,"E16.MirrorCS"),sQuery(id+"F0.wireOp",EDGE,"E17.MirrorCS"),sQuery(id+"F0.wireOp",EDGE,"E18.MirrorCS"),sQuery(id+"F0.wireOp",EDGE,"E19.MirrorCS"),sQuery(id+"F0.wireOp",EDGE,"E20.MirrorCS")])],"isStart":false});
            var sketch = newSketch(context, id + "F15", { "sketchPlane" : qUnion([Q0])});
            skLineSegment(sketch, "E107.0", {"start": v(13.97, -8.97) * mm, "end": v(13.97, 7.62) * mm, "construction": true});
            skLineSegment(sketch, "E108.0", {"start": v(-13.97, -8.97) * mm, "end": v(-13.97, 7.62) * mm, "construction": true});
            skLineSegment(sketch, "E109", {"start": v(13.97, -8.97) * mm, "end": v(-13.97, -8.97) * mm, "construction": true});
            skLineSegment(sketch, "E110", {"start": v(13.97, 7.62) * mm, "end": v(-13.97, 7.62) * mm, "construction": true});
            skLineSegment(sketch, "E111.0", {"start": v(13.9, -8.9) * mm, "end": v(-13.97, -8.9) * mm});
            skLineSegment(sketch, "E111.1", {"start": v(13.9, -8.9) * mm, "end": v(13.9, 7.54) * mm});
            skLineSegment(sketch, "E111.2", {"start": v(13.9, 7.54) * mm, "end": v(-13.97, 7.54) * mm});
            skLineSegment(sketch, "E112.0", {"start": v(-13.9, -8.97) * mm, "end": v(-13.9, 7.62) * mm});
            skSolve(sketch);
        }
        {
            var Q0;
            Q0 = qSketchRegion(id + "F15", true);
            extrude(context, id + "F16", {"entities" : qUnion([Q0]), "depth" : 17.78 * mm});
        }
        {
            var Q0;
            Q0=makeQuery(id+"F16.opExtrude","SWEPT_BODY",BODY,{"disambiguationData":[OSD([sQuery(id+"F15.wireOp",EDGE,"E111.0"),sQuery(id+"F15.wireOp",EDGE,"E111.1"),sQuery(id+"F15.wireOp",EDGE,"E111.2"),sQuery(id+"F15.wireOp",EDGE,"E112.0")])]});
            transform(context, id + "F17", {"entities" : qUnion([Q0]), "transformType" : TransformType.TRANSLATION_3D, "dx" : 0 * mm, "dy" : 0 * mm, "dz" : 50.8 * mm, "makeCopy" : false});
        }
        {
            var Q0;
            Q0=makeQuery(id+"F12.opExtrude","SWEPT_BODY",BODY,{"disambiguationData":[OSD([sQuery(id+"F11.wireOp",EDGE,"E89"),sQuery(id+"F11.wireOp",EDGE,"E90"),sQuery(id+"F11.wireOp",EDGE,"E91"),sQuery(id+"F11.wireOp",EDGE,"E92"),sQuery(id+"F11.wireOp",EDGE,"E93"),sQuery(id+"F11.wireOp",EDGE,"E94"),sQuery(id+"F11.wireOp",EDGE,"E95"),sQuery(id+"F11.wireOp",EDGE,"E96"),sQuery(id+"F11.wireOp",EDGE,"E97"),sQuery(id+"F11.wireOp",EDGE,"E100"),sQuery(id+"F11.wireOp",EDGE,"E101"),sQuery(id+"F11.wireOp",EDGE,"E102")])]});
            transform(context, id + "F18", {"entities" : qUnion([Q0]), "transformType" : TransformType.TRANSLATION_3D, "dx" : 0 * mm, "dy" : 0 * mm, "dz" : 25.4 * mm, "makeCopy" : false});
        }
    });
